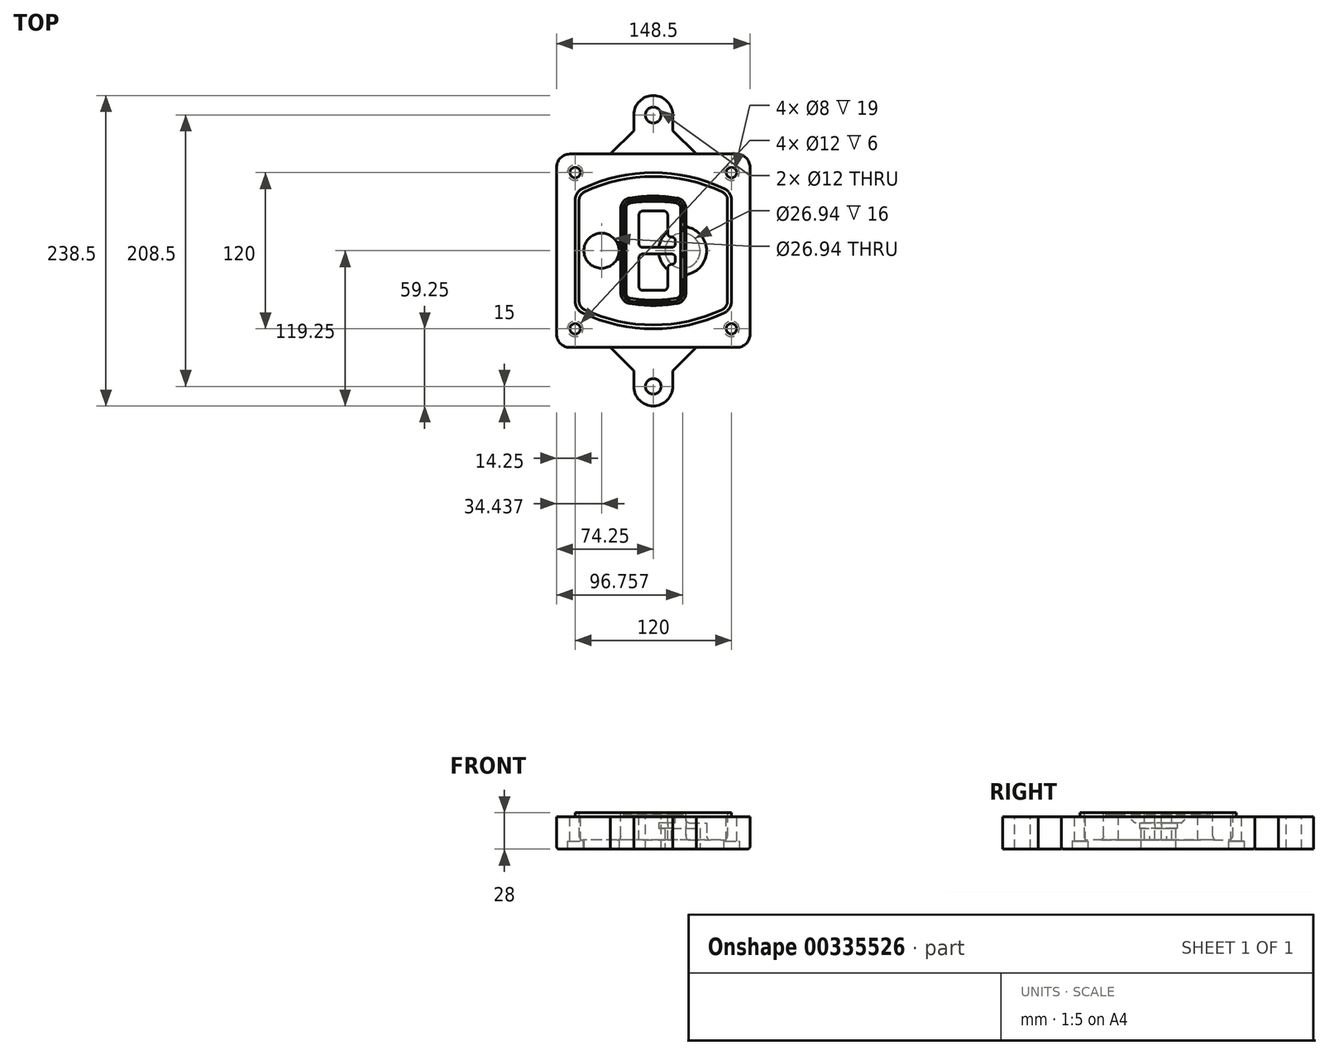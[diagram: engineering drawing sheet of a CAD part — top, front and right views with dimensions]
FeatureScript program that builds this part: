
annotation { "Feature Type Name" : "Feature", "Feature Type Description" : "" }
export const myFeature = defineFeature(function(context is Context, id is Id, definition is map)
    precondition{}
    {
        {
            var Q0;
            Q0=qCreatedBy(makeId("Top.planeOp"),FACE);
            var sketch = newSketch(context, id + "F0", { "sketchPlane" : qUnion([Q0])});
            skPoint(sketch, "E0.rect.middle", {"position": v(0, 0) * mm});
            skLineSegment(sketch, "E1.bottom", {"start": v(-64.25, -74.25) * mm, "end": v(64.25, -74.25) * mm});
            skLineSegment(sketch, "E1.top", {"start": v(-64.25, 74.25) * mm, "end": v(64.25, 74.25) * mm});
            skLineSegment(sketch, "E1.left", {"start": v(-74.25, -64.25) * mm, "end": v(-74.25, 64.25) * mm});
            skLineSegment(sketch, "E1.right", {"start": v(74.25, -64.25) * mm, "end": v(74.25, 64.25) * mm});
            skLineSegment(sketch, "E2", {"start": v(-74.25, 74.25) * mm, "end": v(74.25, -74.25) * mm, "construction": true});
            skLineSegment(sketch, "E3", {"start": v(74.25, 74.25) * mm, "end": v(-74.25, -74.25) * mm, "construction": true});
            skCircle(sketch, "E4", {"center": v(-60, 60) * mm, "radius": 4 * mm});
            skCircle(sketch, "E5", {"center": v(60, 60) * mm, "radius": 4 * mm});
            skCircle(sketch, "E6", {"center": v(60, -60) * mm, "radius": 4 * mm});
            skCircle(sketch, "E7", {"center": v(-60, -60) * mm, "radius": 4 * mm});
            skLineSegment(sketch, "E8", {"start": v(-60, 60) * mm, "end": v(60, 60) * mm, "construction": true});
            skLineSegment(sketch, "E9", {"start": v(60, 60) * mm, "end": v(60, -60) * mm, "construction": true});
            skLineSegment(sketch, "E10", {"start": v(60, -60) * mm, "end": v(-60, -60) * mm, "construction": true});
            skLineSegment(sketch, "E11", {"start": v(-60, -60) * mm, "end": v(-60, 60) * mm, "construction": true});
            skLineSegment(sketch, "E12", {"start": v(-60, 38.83) * mm, "end": v(-60, -38.83) * mm});
            skLineSegment(sketch, "E13", {"start": v(60, 38.83) * mm, "end": v(60, -38.83) * mm});
            skArc(sketch, "E14", {"start": v(54.26, 47.88) * mm, "mid": v(0, 60) * mm, "end": v(-54.26, 47.88) * mm});
            skArc(sketch, "E15", {"start": v(-54.26, -47.88) * mm, "mid": v(0, -60) * mm, "end": v(54.26, -47.88) * mm});
            skLineSegment(sketch, "E16", {"start": v(-60, 0) * mm, "end": v(60, 0) * mm, "construction": true});
            skPoint(sketch, "E17.visualSharp", {"position": v(-60, -45) * mm});
            skArc(sketch, "E17.filletArc", {"start": v(-60, -38.83) * mm, "mid": v(-58.44, -44.2) * mm, "end": v(-54.26, -47.88) * mm});
            skPoint(sketch, "E18.visualSharp", {"position": v(-60, 45) * mm});
            skArc(sketch, "E18.filletArc", {"start": v(-54.26, 47.88) * mm, "mid": v(-58.44, 44.2) * mm, "end": v(-60, 38.83) * mm});
            skPoint(sketch, "E19.visualSharp", {"position": v(60, 45) * mm});
            skArc(sketch, "E19.filletArc", {"start": v(60, 38.83) * mm, "mid": v(58.44, 44.2) * mm, "end": v(54.26, 47.88) * mm});
            skPoint(sketch, "E20.visualSharp", {"position": v(60, -45) * mm});
            skArc(sketch, "E20.filletArc", {"start": v(54.26, -47.88) * mm, "mid": v(58.44, -44.2) * mm, "end": v(60, -38.83) * mm});
            skPoint(sketch, "E21.visualSharp", {"position": v(-74.25, 74.25) * mm});
            skArc(sketch, "E21.filletArc", {"start": v(-64.25, 74.25) * mm, "mid": v(-71.32, 71.32) * mm, "end": v(-74.25, 64.25) * mm});
            skPoint(sketch, "E22.visualSharp", {"position": v(74.25, 74.25) * mm});
            skArc(sketch, "E22.filletArc", {"start": v(74.25, 64.25) * mm, "mid": v(71.32, 71.32) * mm, "end": v(64.25, 74.25) * mm});
            skPoint(sketch, "E23.visualSharp", {"position": v(74.25, -74.25) * mm});
            skArc(sketch, "E23.filletArc", {"start": v(64.25, -74.25) * mm, "mid": v(71.32, -71.32) * mm, "end": v(74.25, -64.25) * mm});
            skPoint(sketch, "E24.visualSharp", {"position": v(-74.25, -74.25) * mm});
            skArc(sketch, "E24.filletArc", {"start": v(-74.25, -64.25) * mm, "mid": v(-71.32, -71.32) * mm, "end": v(-64.25, -74.25) * mm});
            skArc(sketch, "E25.0", {"start": v(57, 38.83) * mm, "mid": v(55.9, 42.58) * mm, "end": v(52.98, 45.17) * mm});
            skLineSegment(sketch, "E25.1", {"start": v(57, 38.83) * mm, "end": v(57, -38.83) * mm});
            skArc(sketch, "E25.2", {"start": v(52.98, -45.17) * mm, "mid": v(55.9, -42.58) * mm, "end": v(57, -38.83) * mm});
            skArc(sketch, "E25.3", {"start": v(-52.98, -45.17) * mm, "mid": v(0, -57) * mm, "end": v(52.98, -45.17) * mm});
            skArc(sketch, "E25.4", {"start": v(-57, -38.83) * mm, "mid": v(-55.9, -42.58) * mm, "end": v(-52.98, -45.17) * mm});
            skArc(sketch, "E25.5", {"start": v(52.98, 45.17) * mm, "mid": v(0, 57) * mm, "end": v(-52.98, 45.17) * mm});
            skLineSegment(sketch, "E25.6", {"start": v(-57, 38.83) * mm, "end": v(-57, -38.83) * mm});
            skArc(sketch, "E25.7", {"start": v(-52.98, 45.17) * mm, "mid": v(-55.9, 42.58) * mm, "end": v(-57, 38.83) * mm});
            skArc(sketch, "E26.0", {"start": v(-55.96, 51.5) * mm, "mid": v(-61.82, 46.33) * mm, "end": v(-64, 38.83) * mm});
            skArc(sketch, "E26.1", {"start": v(55.96, 51.5) * mm, "mid": v(0, 64) * mm, "end": v(-55.96, 51.5) * mm});
            skArc(sketch, "E26.2", {"start": v(64, 38.83) * mm, "mid": v(61.82, 46.33) * mm, "end": v(55.96, 51.5) * mm});
            skLineSegment(sketch, "E26.3", {"start": v(64, 38.83) * mm, "end": v(64, -38.83) * mm});
            skArc(sketch, "E26.4", {"start": v(55.96, -51.5) * mm, "mid": v(61.82, -46.33) * mm, "end": v(64, -38.83) * mm});
            skLineSegment(sketch, "E26.5", {"start": v(-64, 38.83) * mm, "end": v(-64, -38.83) * mm});
            skArc(sketch, "E26.6", {"start": v(-55.96, -51.5) * mm, "mid": v(0, -64) * mm, "end": v(55.96, -51.5) * mm});
            skArc(sketch, "E26.7", {"start": v(-64, -38.83) * mm, "mid": v(-61.82, -46.33) * mm, "end": v(-55.96, -51.5) * mm});
            skSolve(sketch);
        }
        {
            var Q0;
            Q0=makeQuery(id+"F0.imprint","IMPRINT",FACE,{"disambiguationData":[TD([[makeQuery(id+"F0.imprint","IMPRINT",EDGE,{"derivedFrom":sQuery(id+"F0.wireOp",EDGE,"E1.bottom")}),1.0]])]});
            var Q1;
            Q1=makeQuery(id+"F0.imprint","IMPRINT",FACE,{"disambiguationData":[TD([[makeQuery(id+"F0.imprint","IMPRINT",EDGE,{"derivedFrom":sQuery(id+"F0.wireOp",EDGE,"E12")}),1.0]])]});
            var Q2;
            Q2=makeQuery(id+"F0.imprint","IMPRINT",FACE,{"disambiguationData":[TD([[makeQuery(id+"F0.imprint","IMPRINT",EDGE,{"derivedFrom":sQuery(id+"F0.wireOp",EDGE,"E25.0")}),1.0]])]});
            var Q3;
            Q3=makeQuery(id+"F0.imprint","IMPRINT",FACE,{"disambiguationData":[TD([[makeQuery(id+"F0.imprint","IMPRINT",EDGE,{"derivedFrom":sQuery(id+"F0.wireOp",EDGE,"E12")}),-1.0]])]});
            extrude(context, id + "F1", {"entities" : qUnion([Q0, Q1, Q2, Q3]), "oppositeDirection" : true, "depth" : 25 * mm});
        }
        {
            var Q0;
            Q0=makeQuery(id+"F0.imprint","IMPRINT",FACE,{"disambiguationData":[TD([[makeQuery(id+"F0.imprint","IMPRINT",EDGE,{"derivedFrom":sQuery(id+"F0.wireOp",EDGE,"E12")}),1.0]])]});
            extrude(context, id + "F2", {"entities" : qUnion([Q0]), "operationType" : NewBodyOperationType.ADD, "depth" : 3 * mm});
        }
        {
            var Q0;
            Q0=makeQuery(id+"F0.imprint","IMPRINT",FACE,{"disambiguationData":[TD([[makeQuery(id+"F0.imprint","IMPRINT",EDGE,{"derivedFrom":sQuery(id+"F0.wireOp",EDGE,"E25.0")}),1.0]])]});
            extrude(context, id + "F3", {"entities" : qUnion([Q0]), "operationType" : NewBodyOperationType.REMOVE, "oppositeDirection" : true, "depth" : 18 * mm});
        }
        {
            var Q0;
            Q0=makeQuery(id+"F2.opExtrude","CAP_FACE",FACE,{"disambiguationData":[OSD([sQuery(id+"F0.wireOp",EDGE,"E12"),sQuery(id+"F0.wireOp",EDGE,"E13"),sQuery(id+"F0.wireOp",EDGE,"E14"),sQuery(id+"F0.wireOp",EDGE,"E15"),sQuery(id+"F0.wireOp",EDGE,"E17.filletArc"),sQuery(id+"F0.wireOp",EDGE,"E18.filletArc"),sQuery(id+"F0.wireOp",EDGE,"E19.filletArc"),sQuery(id+"F0.wireOp",EDGE,"E20.filletArc"),sQuery(id+"F0.wireOp",EDGE,"E25.0"),sQuery(id+"F0.wireOp",EDGE,"E25.1"),sQuery(id+"F0.wireOp",EDGE,"E25.2"),sQuery(id+"F0.wireOp",EDGE,"E25.3"),sQuery(id+"F0.wireOp",EDGE,"E25.4"),sQuery(id+"F0.wireOp",EDGE,"E25.5"),sQuery(id+"F0.wireOp",EDGE,"E25.6"),sQuery(id+"F0.wireOp",EDGE,"E25.7")])],"isStart":false});
            var sketch = newSketch(context, id + "F4", { "sketchPlane" : qUnion([Q0])});
            skArc(sketch, "E27.0", {"start": v(-18.34, -40.45) * mm, "mid": v(0, -42) * mm, "end": v(18.34, -40.45) * mm});
            skArc(sketch, "E28.0", {"start": v(18.34, 40.45) * mm, "mid": v(0, 42) * mm, "end": v(-18.34, 40.45) * mm});
            skLineSegment(sketch, "E29", {"start": v(-25, 32.57) * mm, "end": v(-25, -32.57) * mm});
            skLineSegment(sketch, "E30", {"start": v(25, 32.57) * mm, "end": v(25, -32.57) * mm});
            skLineSegment(sketch, "E31", {"start": v(-25, 39.1) * mm, "end": v(25, 39.1) * mm, "construction": true});
            skLineSegment(sketch, "E32", {"start": v(-25, -39.1) * mm, "end": v(25, -39.1) * mm, "construction": true});
            skPoint(sketch, "E33.visualSharp", {"position": v(-25, 39.1) * mm});
            skArc(sketch, "E33.filletArc", {"start": v(-18.34, 40.45) * mm, "mid": v(-23.11, 37.73) * mm, "end": v(-25, 32.57) * mm});
            skPoint(sketch, "E34.visualSharp", {"position": v(25, 39.1) * mm});
            skArc(sketch, "E34.filletArc", {"start": v(25, 32.57) * mm, "mid": v(23.11, 37.73) * mm, "end": v(18.34, 40.45) * mm});
            skPoint(sketch, "E35.visualSharp", {"position": v(25, -39.1) * mm});
            skArc(sketch, "E35.filletArc", {"start": v(18.34, -40.45) * mm, "mid": v(23.11, -37.73) * mm, "end": v(25, -32.57) * mm});
            skPoint(sketch, "E36.visualSharp", {"position": v(-25, -39.1) * mm});
            skArc(sketch, "E36.filletArc", {"start": v(-25, -32.57) * mm, "mid": v(-23.11, -37.73) * mm, "end": v(-18.34, -40.45) * mm});
            skArc(sketch, "E37.0", {"start": v(52.98, 45.17) * mm, "mid": v(0, 57) * mm, "end": v(-52.98, 45.17) * mm});
            skArc(sketch, "E37.1", {"start": v(-52.98, 45.17) * mm, "mid": v(-55.9, 42.58) * mm, "end": v(-57, 38.83) * mm});
            skLineSegment(sketch, "E37.2", {"start": v(-57, 38.83) * mm, "end": v(-57, -38.83) * mm});
            skArc(sketch, "E37.3", {"start": v(-57, -38.83) * mm, "mid": v(-55.9, -42.58) * mm, "end": v(-52.98, -45.17) * mm});
            skArc(sketch, "E37.4", {"start": v(-52.98, -45.17) * mm, "mid": v(0, -57) * mm, "end": v(52.98, -45.17) * mm});
            skArc(sketch, "E37.5", {"start": v(52.98, -45.17) * mm, "mid": v(55.9, -42.58) * mm, "end": v(57, -38.83) * mm});
            skLineSegment(sketch, "E37.6", {"start": v(57, 38.83) * mm, "end": v(57, -38.83) * mm});
            skArc(sketch, "E37.7", {"start": v(57, 38.83) * mm, "mid": v(55.9, 42.58) * mm, "end": v(52.98, 45.17) * mm});
            skLineSegment(sketch, "E38.0", {"start": v(23, 32.57) * mm, "end": v(23, -32.57) * mm});
            skArc(sketch, "E38.1", {"start": v(18, -38.48) * mm, "mid": v(21.58, -36.44) * mm, "end": v(23, -32.57) * mm});
            skArc(sketch, "E38.2", {"start": v(-18, -38.48) * mm, "mid": v(0, -40) * mm, "end": v(18, -38.48) * mm});
            skArc(sketch, "E38.3", {"start": v(-23, -32.57) * mm, "mid": v(-21.58, -36.44) * mm, "end": v(-18, -38.48) * mm});
            skLineSegment(sketch, "E38.4", {"start": v(-23, 32.57) * mm, "end": v(-23, -32.57) * mm});
            skArc(sketch, "E38.5", {"start": v(23, 32.57) * mm, "mid": v(21.58, 36.44) * mm, "end": v(18, 38.48) * mm});
            skArc(sketch, "E38.6", {"start": v(-18, 38.48) * mm, "mid": v(-21.58, 36.44) * mm, "end": v(-23, 32.57) * mm});
            skArc(sketch, "E38.7", {"start": v(18, 38.48) * mm, "mid": v(0, 40) * mm, "end": v(-18, 38.48) * mm});
            skArc(sketch, "E39.0", {"start": v(21, 32.57) * mm, "mid": v(20.06, 35.15) * mm, "end": v(17.67, 36.5) * mm});
            skLineSegment(sketch, "E39.1", {"start": v(21, 32.57) * mm, "end": v(21, -32.57) * mm});
            skArc(sketch, "E39.2", {"start": v(17.67, -36.5) * mm, "mid": v(20.06, -35.15) * mm, "end": v(21, -32.57) * mm});
            skArc(sketch, "E39.3", {"start": v(-17.67, -36.5) * mm, "mid": v(0, -38) * mm, "end": v(17.67, -36.5) * mm});
            skArc(sketch, "E39.4", {"start": v(-21, -32.57) * mm, "mid": v(-20.06, -35.15) * mm, "end": v(-17.67, -36.5) * mm});
            skArc(sketch, "E39.5", {"start": v(17.67, 36.5) * mm, "mid": v(0, 38) * mm, "end": v(-17.67, 36.5) * mm});
            skLineSegment(sketch, "E39.6", {"start": v(-21, 32.57) * mm, "end": v(-21, -32.57) * mm});
            skArc(sketch, "E39.7", {"start": v(-17.67, 36.5) * mm, "mid": v(-20.06, 35.15) * mm, "end": v(-21, 32.57) * mm});
            skLineSegment(sketch, "E40", {"start": v(-25, 0) * mm, "end": v(25, 0) * mm, "construction": true});
            skLineSegment(sketch, "E41", {"start": v(-11, 5.5) * mm, "end": v(-11, 27.5) * mm});
            skLineSegment(sketch, "E42", {"start": v(-8, 30.5) * mm, "end": v(8, 30.5) * mm});
            skLineSegment(sketch, "E43", {"start": v(11, 27.5) * mm, "end": v(11, 13.5) * mm});
            skLineSegment(sketch, "E44", {"start": v(14, 10.5) * mm, "end": v(14, 10.5) * mm});
            skLineSegment(sketch, "E45", {"start": v(17, 7.5) * mm, "end": v(17, 5.5) * mm});
            skLineSegment(sketch, "E46", {"start": v(14, 2.5) * mm, "end": v(-8, 2.5) * mm});
            skPoint(sketch, "E47.visualSharp", {"position": v(-11, 30.5) * mm});
            skArc(sketch, "E47.filletArc", {"start": v(-8, 30.5) * mm, "mid": v(-10.12, 29.62) * mm, "end": v(-11, 27.5) * mm});
            skPoint(sketch, "E48.visualSharp", {"position": v(11, 30.5) * mm});
            skArc(sketch, "E48.filletArc", {"start": v(11, 27.5) * mm, "mid": v(10.12, 29.62) * mm, "end": v(8, 30.5) * mm});
            skPoint(sketch, "E49.visualSharp", {"position": v(11, 10.5) * mm});
            skArc(sketch, "E49.filletArc", {"start": v(11, 13.5) * mm, "mid": v(11.88, 11.38) * mm, "end": v(14, 10.5) * mm});
            skPoint(sketch, "E50.visualSharp", {"position": v(17, 10.5) * mm});
            skArc(sketch, "E50.filletArc", {"start": v(17, 7.5) * mm, "mid": v(16.12, 9.62) * mm, "end": v(14, 10.5) * mm});
            skPoint(sketch, "E51.visualSharp", {"position": v(17, 2.5) * mm});
            skArc(sketch, "E51.filletArc", {"start": v(14, 2.5) * mm, "mid": v(16.12, 3.38) * mm, "end": v(17, 5.5) * mm});
            skPoint(sketch, "E52.visualSharp", {"position": v(-11, 2.5) * mm});
            skArc(sketch, "E52.filletArc", {"start": v(-11, 5.5) * mm, "mid": v(-10.12, 3.38) * mm, "end": v(-8, 2.5) * mm});
            skLineSegment(sketch, "E53.0.MirrorCS", {"start": v(14, -2.5) * mm, "end": v(-8, -2.5) * mm});
            skArc(sketch, "E54.0.MirrorCS", {"start": v(-11, -5.5) * mm, "mid": v(-10.12, -3.38) * mm, "end": v(-8, -2.5) * mm});
            skLineSegment(sketch, "E55.0.MirrorCS", {"start": v(-11, -5.5) * mm, "end": v(-11, -27.5) * mm});
            skArc(sketch, "E56.0.MirrorCS", {"start": v(-8, -30.5) * mm, "mid": v(-10.12, -29.62) * mm, "end": v(-11, -27.5) * mm});
            skLineSegment(sketch, "E57.0.MirrorCS", {"start": v(-8, -30.5) * mm, "end": v(8, -30.5) * mm});
            skArc(sketch, "E58.0.MirrorCS", {"start": v(11, -27.5) * mm, "mid": v(10.12, -29.62) * mm, "end": v(8, -30.5) * mm});
            skLineSegment(sketch, "E59.0.MirrorCS", {"start": v(11, -27.5) * mm, "end": v(11, -13.5) * mm});
            skArc(sketch, "E60.0.MirrorCS", {"start": v(11, -13.5) * mm, "mid": v(11.88, -11.38) * mm, "end": v(14, -10.5) * mm});
            skArc(sketch, "E61.0.MirrorCS", {"start": v(17, -7.5) * mm, "mid": v(16.12, -9.62) * mm, "end": v(14, -10.5) * mm});
            skLineSegment(sketch, "E62.0.MirrorCS", {"start": v(17, -7.5) * mm, "end": v(17, -5.5) * mm});
            skArc(sketch, "E63.0.MirrorCS", {"start": v(14, -2.5) * mm, "mid": v(16.12, -3.38) * mm, "end": v(17, -5.5) * mm});
            skSolve(sketch);
        }
        {
            var Q0;
            Q0=makeQuery(id+"F4.imprint","IMPRINT",FACE,{"disambiguationData":[TD([[makeQuery(id+"F4.imprint","IMPRINT",EDGE,{"derivedFrom":sQuery(id+"F4.wireOp",EDGE,"E27.0")}),1.0]])]});
            var Q1;
            Q1=makeQuery(id+"F4.imprint","IMPRINT",FACE,{"disambiguationData":[TD([[makeQuery(id+"F4.imprint","IMPRINT",EDGE,{"derivedFrom":sQuery(id+"F4.wireOp",EDGE,"E38.0")}),-1.0]])]});
            var Q2;
            Q2=makeQuery(id+"F4.imprint","IMPRINT",FACE,{"disambiguationData":[TD([[makeQuery(id+"F4.imprint","IMPRINT",EDGE,{"derivedFrom":sQuery(id+"F4.wireOp",EDGE,"E39.0")}),1.0]])]});
            extrude(context, id + "F5", {"entities" : qUnion([Q0, Q1, Q2]), "operationType" : NewBodyOperationType.ADD, "endBound" : BoundingType.UP_TO_NEXT, "oppositeDirection" : true, "depth" : 25 * mm});
        }
        {
            var Q0;
            Q0=makeQuery(id+"F4.imprint","IMPRINT",FACE,{"disambiguationData":[TD([[makeQuery(id+"F4.imprint","IMPRINT",EDGE,{"derivedFrom":sQuery(id+"F4.wireOp",EDGE,"E38.0")}),-1.0]])]});
            extrude(context, id + "F6", {"entities" : qUnion([Q0]), "operationType" : NewBodyOperationType.REMOVE, "oppositeDirection" : true, "depth" : 2 * mm});
        }
        {
            var Q0;
            Q0=makeQuery(id+"F1.opExtrude","CAP_FACE",FACE,{"disambiguationData":[OSD([sQuery(id+"F0.wireOp",EDGE,"E1.bottom"),sQuery(id+"F0.wireOp",EDGE,"E1.top"),sQuery(id+"F0.wireOp",EDGE,"E1.left"),sQuery(id+"F0.wireOp",EDGE,"E1.right"),sQuery(id+"F0.wireOp",EDGE,"E4"),sQuery(id+"F0.wireOp",EDGE,"E5"),sQuery(id+"F0.wireOp",EDGE,"E6"),sQuery(id+"F0.wireOp",EDGE,"E7"),sQuery(id+"F0.wireOp",EDGE,"E21.filletArc"),sQuery(id+"F0.wireOp",EDGE,"E22.filletArc"),sQuery(id+"F0.wireOp",EDGE,"E23.filletArc"),sQuery(id+"F0.wireOp",EDGE,"E24.filletArc")])],"isStart":false});
            var sketch = newSketch(context, id + "F7", { "sketchPlane" : qUnion([Q0])});
            skCircle(sketch, "E64", {"center": v(22.5, 0) * mm, "radius": 13.47 * mm});
            skCircle(sketch, "E65", {"center": v(-39.81, 0) * mm, "radius": 13.47 * mm});
            skLineSegment(sketch, "E66", {"start": v(74.25, 0) * mm, "end": v(-74.25, 0) * mm});
            skCircle(sketch, "E67", {"center": v(22.5, 0) * mm, "radius": 18.47 * mm});
            skCircle(sketch, "E68", {"center": v(60, -60) * mm, "radius": 6 * mm});
            skCircle(sketch, "E69", {"center": v(-60, -60) * mm, "radius": 6 * mm});
            skCircle(sketch, "E70", {"center": v(-60, 60) * mm, "radius": 6 * mm});
            skCircle(sketch, "E71", {"center": v(60, 60) * mm, "radius": 6 * mm});
            skSolve(sketch);
        }
        {
            var Q0;
            {var subQ1=sQuery(id+"F7.wireOp",EDGE,"E66");var subQ4=sQuery(id+"F7.wireOp",EDGE,"E64");var subQ6=makeQuery(id+"F7.imprint","INTERSECT",VERTEX,{"disambiguationData":[OD(0.0)],"derivedFrom":[subQ4,subQ1]});Q0=makeQuery(id+"F7.imprint","IMPRINT",FACE,{"disambiguationData":[TD([[makeQuery(id+"F7.imprint","IMPRINT",EDGE,{"disambiguationData":[TD([[subQ6,-1.0]])],"derivedFrom":subQ4}),-1.0]])]});}
            var Q1;
            {var subQ0=sQuery(id+"F7.wireOp",EDGE,"E66");var subQ1=sQuery(id+"F7.wireOp",EDGE,"E64");var subQ3=makeQuery(id+"F7.imprint","INTERSECT",VERTEX,{"disambiguationData":[OD(0.0)],"derivedFrom":[subQ1,subQ0]});Q1=makeQuery(id+"F7.imprint","IMPRINT",FACE,{"disambiguationData":[TD([[makeQuery(id+"F7.imprint","IMPRINT",EDGE,{"disambiguationData":[TD([[subQ3,-1.0]])],"derivedFrom":subQ1}),1.0]])]});}
            var Q2;
            {var subQ0=sQuery(id+"F7.wireOp",EDGE,"E66");var subQ1=sQuery(id+"F7.wireOp",EDGE,"E64");var subQ3=makeQuery(id+"F7.imprint","INTERSECT",VERTEX,{"disambiguationData":[OD(0.0)],"derivedFrom":[subQ1,subQ0]});Q2=makeQuery(id+"F7.imprint","IMPRINT",FACE,{"disambiguationData":[TD([[makeQuery(id+"F7.imprint","IMPRINT",EDGE,{"disambiguationData":[TD([[subQ3,1.0]])],"derivedFrom":subQ1}),1.0]])]});}
            var Q3;
            {var subQ1=sQuery(id+"F7.wireOp",EDGE,"E66");var subQ4=sQuery(id+"F7.wireOp",EDGE,"E64");var subQ6=makeQuery(id+"F7.imprint","INTERSECT",VERTEX,{"disambiguationData":[OD(0.0)],"derivedFrom":[subQ4,subQ1]});Q3=makeQuery(id+"F7.imprint","IMPRINT",FACE,{"disambiguationData":[TD([[makeQuery(id+"F7.imprint","IMPRINT",EDGE,{"disambiguationData":[TD([[subQ6,1.0]])],"derivedFrom":subQ4}),-1.0]])]});}
            extrude(context, id + "F8", {"entities" : qUnion([Q0, Q1, Q2, Q3]), "operationType" : NewBodyOperationType.ADD, "oppositeDirection" : true, "depth" : 20 * mm});
        }
        {
            var Q0;
            {var subQ0=sQuery(id+"F7.wireOp",EDGE,"E66");var subQ1=sQuery(id+"F7.wireOp",EDGE,"E64");var subQ3=makeQuery(id+"F7.imprint","INTERSECT",VERTEX,{"disambiguationData":[OD(0.0)],"derivedFrom":[subQ1,subQ0]});Q0=makeQuery(id+"F7.imprint","IMPRINT",FACE,{"disambiguationData":[TD([[makeQuery(id+"F7.imprint","IMPRINT",EDGE,{"disambiguationData":[TD([[subQ3,-1.0]])],"derivedFrom":subQ1}),1.0]])]});}
            var Q1;
            {var subQ0=sQuery(id+"F7.wireOp",EDGE,"E66");var subQ1=sQuery(id+"F7.wireOp",EDGE,"E64");var subQ3=makeQuery(id+"F7.imprint","INTERSECT",VERTEX,{"disambiguationData":[OD(0.0)],"derivedFrom":[subQ1,subQ0]});Q1=makeQuery(id+"F7.imprint","IMPRINT",FACE,{"disambiguationData":[TD([[makeQuery(id+"F7.imprint","IMPRINT",EDGE,{"disambiguationData":[TD([[subQ3,1.0]])],"derivedFrom":subQ1}),1.0]])]});}
            extrude(context, id + "F9", {"entities" : qUnion([Q0, Q1]), "operationType" : NewBodyOperationType.REMOVE, "oppositeDirection" : true, "depth" : 16 * mm});
        }
        {
            var Q0;
            {var subQ0=sQuery(id+"F7.wireOp",EDGE,"E66");var subQ1=sQuery(id+"F7.wireOp",EDGE,"E65");var subQ3=makeQuery(id+"F7.imprint","INTERSECT",VERTEX,{"disambiguationData":[OD(0.0)],"derivedFrom":[subQ1,subQ0]});Q0=makeQuery(id+"F7.imprint","IMPRINT",FACE,{"disambiguationData":[TD([[makeQuery(id+"F7.imprint","IMPRINT",EDGE,{"disambiguationData":[TD([[subQ3,-1.0]])],"derivedFrom":subQ1}),1.0]])]});}
            var Q1;
            {var subQ0=sQuery(id+"F7.wireOp",EDGE,"E66");var subQ1=sQuery(id+"F7.wireOp",EDGE,"E65");var subQ3=makeQuery(id+"F7.imprint","INTERSECT",VERTEX,{"disambiguationData":[OD(0.0)],"derivedFrom":[subQ1,subQ0]});Q1=makeQuery(id+"F7.imprint","IMPRINT",FACE,{"disambiguationData":[TD([[makeQuery(id+"F7.imprint","IMPRINT",EDGE,{"disambiguationData":[TD([[subQ3,1.0]])],"derivedFrom":subQ1}),1.0]])]});}
            extrude(context, id + "F10", {"entities" : qUnion([Q0, Q1]), "operationType" : NewBodyOperationType.REMOVE, "oppositeDirection" : true, "depth" : 25 * mm});
        }
        {
            var Q0;
            Q0=makeQuery(id+"F7.imprint","IMPRINT",FACE,{"disambiguationData":[TD([[makeQuery(id+"F7.imprint","IMPRINT",EDGE,{"derivedFrom":sQuery(id+"F7.wireOp",EDGE,"E68")}),1.0]])]});
            var Q1;
            Q1=makeQuery(id+"F7.imprint","IMPRINT",FACE,{"disambiguationData":[TD([[makeQuery(id+"F7.imprint","IMPRINT",EDGE,{"derivedFrom":makeQuery(id+"F1.opExtrude","CAP_EDGE",EDGE,{"disambiguationData":[OSD([sQuery(id+"F0.wireOp",EDGE,"E5")])],"isStart":false})}),-1.0]])]});
            var Q2;
            Q2=makeQuery(id+"F7.imprint","IMPRINT",FACE,{"disambiguationData":[TD([[makeQuery(id+"F7.imprint","IMPRINT",EDGE,{"derivedFrom":sQuery(id+"F7.wireOp",EDGE,"E69")}),1.0]])]});
            var Q3;
            Q3=makeQuery(id+"F7.imprint","IMPRINT",FACE,{"disambiguationData":[TD([[makeQuery(id+"F7.imprint","IMPRINT",EDGE,{"derivedFrom":makeQuery(id+"F1.opExtrude","CAP_EDGE",EDGE,{"disambiguationData":[OSD([sQuery(id+"F0.wireOp",EDGE,"E4")])],"isStart":false})}),-1.0]])]});
            var Q4;
            Q4=makeQuery(id+"F7.imprint","IMPRINT",FACE,{"disambiguationData":[TD([[makeQuery(id+"F7.imprint","IMPRINT",EDGE,{"derivedFrom":sQuery(id+"F7.wireOp",EDGE,"E70")}),1.0]])]});
            var Q5;
            Q5=makeQuery(id+"F7.imprint","IMPRINT",FACE,{"disambiguationData":[TD([[makeQuery(id+"F7.imprint","IMPRINT",EDGE,{"derivedFrom":makeQuery(id+"F1.opExtrude","CAP_EDGE",EDGE,{"disambiguationData":[OSD([sQuery(id+"F0.wireOp",EDGE,"E7")])],"isStart":false})}),-1.0]])]});
            var Q6;
            Q6=makeQuery(id+"F7.imprint","IMPRINT",FACE,{"disambiguationData":[TD([[makeQuery(id+"F7.imprint","IMPRINT",EDGE,{"derivedFrom":sQuery(id+"F7.wireOp",EDGE,"E71")}),1.0]])]});
            var Q7;
            Q7=makeQuery(id+"F7.imprint","IMPRINT",FACE,{"disambiguationData":[TD([[makeQuery(id+"F7.imprint","IMPRINT",EDGE,{"derivedFrom":makeQuery(id+"F1.opExtrude","CAP_EDGE",EDGE,{"disambiguationData":[OSD([sQuery(id+"F0.wireOp",EDGE,"E6")])],"isStart":false})}),-1.0]])]});
            extrude(context, id + "F11", {"entities" : qUnion([Q0, Q1, Q2, Q3, Q4, Q5, Q6, Q7]), "operationType" : NewBodyOperationType.REMOVE, "oppositeDirection" : true, "depth" : 6 * mm});
        }
        {
            var Q0;
            Q0=makeQuery(id+"F9.boolean.opBoolean","COPY",FACE,{"derivedFrom":makeQuery(id+"F9.opExtrude","CAP_FACE",FACE,{"disambiguationData":[OSD([sQuery(id+"F7.wireOp",EDGE,"E64")])],"isStart":false})});
            var sketch = newSketch(context, id + "F12", { "sketchPlane" : qUnion([Q0])});
            skArc(sketch, "E72.0", {"start": v(11, 14.45) * mm, "mid": v(6.45, 9.13) * mm, "end": v(4.2, 2.5) * mm});
            skArc(sketch, "E72.1", {"start": v(4.2, -2.5) * mm, "mid": v(6.45, -9.13) * mm, "end": v(11, -14.45) * mm});
            skLineSegment(sketch, "E73", {"start": v(4.2, -2.5) * mm, "end": v(14, -2.5) * mm});
            skLineSegment(sketch, "E74.0", {"start": v(14, 2.5) * mm, "end": v(4.2, 2.5) * mm});
            skArc(sketch, "E74.1", {"start": v(14, 2.5) * mm, "mid": v(16.12, 3.38) * mm, "end": v(17, 5.5) * mm});
            skLineSegment(sketch, "E74.2", {"start": v(17, 7.5) * mm, "end": v(17, 5.5) * mm});
            skArc(sketch, "E74.3", {"start": v(17, 7.5) * mm, "mid": v(16.12, 9.62) * mm, "end": v(14, 10.5) * mm});
            skArc(sketch, "E74.4", {"start": v(11, 13.5) * mm, "mid": v(11.88, 11.38) * mm, "end": v(14, 10.5) * mm});
            skLineSegment(sketch, "E74.5", {"start": v(11, 14.45) * mm, "end": v(11, 13.5) * mm});
            skLineSegment(sketch, "E74.7", {"start": v(14, -2.5) * mm, "end": v(4.2, -2.5) * mm});
            skArc(sketch, "E74.8", {"start": v(14, -2.5) * mm, "mid": v(16.12, -3.38) * mm, "end": v(17, -5.5) * mm});
            skLineSegment(sketch, "E74.9", {"start": v(17, -7.5) * mm, "end": v(17, -5.5) * mm});
            skArc(sketch, "E74.10", {"start": v(17, -7.5) * mm, "mid": v(16.12, -9.62) * mm, "end": v(14, -10.5) * mm});
            skArc(sketch, "E74.11", {"start": v(11, -13.5) * mm, "mid": v(11.88, -11.38) * mm, "end": v(14, -10.5) * mm});
            skLineSegment(sketch, "E74.12", {"start": v(11, -14.45) * mm, "end": v(11, -13.5) * mm});
            skPoint(sketch, "E75.orphan", {"position": v(11, -27.5) * mm});
            skPoint(sketch, "E76.orphan", {"position": v(-8, -2.5) * mm});
            skPoint(sketch, "E77.orphan", {"position": v(-8, 2.5) * mm});
            skPoint(sketch, "E78.orphan", {"position": v(11, 27.5) * mm});
            skSolve(sketch);
        }
        {
            var Q0;
            {var subQ7=sQuery(id+"F12.wireOp",EDGE,"E72.0");var subQ14=sQuery(id+"F12.wireOp",EDGE,"E72.1");var subQ16=sQuery(id+"F12.wireOp",EDGE,"E74.1");var subQ18=sQuery(id+"F12.wireOp",EDGE,"E74.8");Q0=qUnion([makeQuery(id+"F12.imprint","IMPRINT",FACE,{"disambiguationData":[TD([[makeQuery(id+"F12.imprint","IMPRINT",EDGE,{"derivedFrom":subQ7}),1.0]])]}),makeQuery(id+"F12.imprint","IMPRINT",FACE,{"disambiguationData":[TD([[makeQuery(id+"F12.imprint","IMPRINT",EDGE,{"derivedFrom":subQ14}),1.0]])]}),makeQuery(id+"F12.imprint","IMPRINT",FACE,{"disambiguationData":[TD([[makeQuery(id+"F12.imprint","IMPRINT",EDGE,{"derivedFrom":subQ16}),1.0]])]}),makeQuery(id+"F12.imprint","IMPRINT",FACE,{"disambiguationData":[TD([[makeQuery(id+"F12.imprint","IMPRINT",EDGE,{"derivedFrom":subQ18}),-1.0]])]})]);}
            var Q1;
            Q1=makeQuery(id+"F5.boolean.opBoolean","SPLIT",FACE,{"disambiguationData":[TD([makeQuery(id+"F5.opExtrude","SWEPT_FACE",FACE,{"disambiguationData":[OSD([sQuery(id+"F4.wireOp",EDGE,"E41")])]})])],"derivedFrom":makeQuery(id+"F3.boolean.opBoolean","COPY",FACE,{"derivedFrom":makeQuery(id+"F3.opExtrude","CAP_FACE",FACE,{"disambiguationData":[OSD([sQuery(id+"F0.wireOp",EDGE,"E25.0"),sQuery(id+"F0.wireOp",EDGE,"E25.1"),sQuery(id+"F0.wireOp",EDGE,"E25.2"),sQuery(id+"F0.wireOp",EDGE,"E25.3"),sQuery(id+"F0.wireOp",EDGE,"E25.4"),sQuery(id+"F0.wireOp",EDGE,"E25.5"),sQuery(id+"F0.wireOp",EDGE,"E25.6"),sQuery(id+"F0.wireOp",EDGE,"E25.7")])],"isStart":false})})});
            extrude(context, id + "F13", {"entities" : qUnion([Q0]), "operationType" : NewBodyOperationType.REMOVE, "endBound" : BoundingType.UP_TO_SURFACE, "endBoundEntityFace" : qUnion([Q1]), "depth" : 25 * mm});
        }
        {
            var Q0;
            Q0=makeQuery(id+"F3.boolean.opBoolean","COPY",EDGE,{"derivedFrom":makeQuery(id+"F3.opExtrude","CAP_EDGE",EDGE,{"disambiguationData":[OSD([sQuery(id+"F0.wireOp",EDGE,"E25.6")])],"isStart":false})});
            var Q1;
            Q1=makeQuery(id+"F8.boolean.opBoolean","INTERSECT",EDGE,{"derivedFrom":[makeQuery(id+"F5.opExtrude","SWEPT_FACE",FACE,{"disambiguationData":[OSD([sQuery(id+"F4.wireOp",EDGE,"E30")])]}),makeQuery(id+"F8.opExtrude","CAP_FACE",FACE,{"disambiguationData":[OSD([sQuery(id+"F7.wireOp",EDGE,"E67")])],"isStart":false})]});
            var Q2;
            Q2=makeQuery(id+"F8.boolean.opBoolean","INTERSECT",EDGE,{"disambiguationData":[OD(1.0)],"derivedFrom":[makeQuery(id+"F5.opExtrude","SWEPT_FACE",FACE,{"disambiguationData":[OSD([sQuery(id+"F4.wireOp",EDGE,"E30")])]}),makeQuery(id+"F8.opExtrude","SWEPT_FACE",FACE,{"disambiguationData":[OSD([sQuery(id+"F7.wireOp",EDGE,"E67")])]})]});
            var Q3;
            {var subQ0=sQuery(id+"F4.wireOp",EDGE,"E30");Q3=makeQuery(id+"F8.boolean.opBoolean","SPLIT",EDGE,{"disambiguationData":[TD([makeQuery(id+"F5.opExtrude","SWEPT_FACE",FACE,{"disambiguationData":[OSD([sQuery(id+"F4.wireOp",EDGE,"E35.filletArc")])]})])],"derivedFrom":makeQuery(id+"F5.opExtrude","CAP_EDGE",EDGE,{"disambiguationData":[OSD([subQ0])],"isStart":false})});}
            var Q4;
            {var subQ0=sQuery(id+"F0.wireOp",EDGE,"E25.7");var subQ1=sQuery(id+"F0.wireOp",EDGE,"E25.1");var subQ2=sQuery(id+"F0.wireOp",EDGE,"E25.6");var subQ3=sQuery(id+"F0.wireOp",EDGE,"E25.5");var subQ4=sQuery(id+"F0.wireOp",EDGE,"E25.4");var subQ5=sQuery(id+"F0.wireOp",EDGE,"E25.0");var subQ6=sQuery(id+"F0.wireOp",EDGE,"E25.2");var subQ7=sQuery(id+"F0.wireOp",EDGE,"E25.3");Q4=makeQuery(id+"F8.boolean.opBoolean","INTERSECT",EDGE,{"derivedFrom":[makeQuery(id+"F5.boolean.opBoolean","SPLIT",FACE,{"disambiguationData":[TD([makeQuery(id+"F2.opExtrude","SWEPT_FACE",FACE,{"disambiguationData":[OSD([subQ5])]})])],"derivedFrom":makeQuery(id+"F3.boolean.opBoolean","COPY",FACE,{"derivedFrom":makeQuery(id+"F3.opExtrude","CAP_FACE",FACE,{"disambiguationData":[OSD([subQ5,subQ1,subQ6,subQ7,subQ4,subQ3,subQ2,subQ0])],"isStart":false})})}),makeQuery(id+"F8.opExtrude","SWEPT_FACE",FACE,{"disambiguationData":[OSD([sQuery(id+"F7.wireOp",EDGE,"E67")])]})]});}
            var Q5;
            Q5=makeQuery(id+"F8.boolean.opBoolean","INTERSECT",EDGE,{"disambiguationData":[OD(0.0)],"derivedFrom":[makeQuery(id+"F5.opExtrude","SWEPT_FACE",FACE,{"disambiguationData":[OSD([sQuery(id+"F4.wireOp",EDGE,"E30")])]}),makeQuery(id+"F8.opExtrude","SWEPT_FACE",FACE,{"disambiguationData":[OSD([sQuery(id+"F7.wireOp",EDGE,"E67")])]})]});
            fillet(context, id + "F14", {"entities" : qUnion([Q0, Q1, Q2, Q3, Q4, Q5]), "radius" : 3 * mm, "tangentPropagation" : true, "allowEdgeOverflow" : false});
        }
        {
            var Q0;
            Q0=makeQuery(id+"F1.opExtrude","CAP_EDGE",EDGE,{"disambiguationData":[OSD([sQuery(id+"F0.wireOp",EDGE,"E1.bottom")])],"isStart":false});
            fillet(context, id + "F15", {"entities" : qUnion([Q0]), "radius" : 2 * mm, "tangentPropagation" : true, "allowEdgeOverflow" : false});
        }
        {
            var Q0;
            {var subQ0=sQuery(id+"F0.wireOp",EDGE,"E21.filletArc");var subQ1=sQuery(id+"F0.wireOp",EDGE,"E7");var subQ2=sQuery(id+"F0.wireOp",EDGE,"E6");var subQ3=sQuery(id+"F0.wireOp",EDGE,"E5");var subQ4=sQuery(id+"F0.wireOp",EDGE,"E4");var subQ5=sQuery(id+"F0.wireOp",EDGE,"E22.filletArc");var subQ6=sQuery(id+"F0.wireOp",EDGE,"E1.bottom");var subQ7=sQuery(id+"F0.wireOp",EDGE,"E1.right");var subQ8=sQuery(id+"F0.wireOp",EDGE,"E1.top");var subQ9=sQuery(id+"F0.wireOp",EDGE,"E1.left");var subQ10=sQuery(id+"F0.wireOp",EDGE,"E23.filletArc");var subQ11=sQuery(id+"F0.wireOp",EDGE,"E24.filletArc");Q0=makeQuery(id+"F2.boolean.opBoolean","SPLIT",FACE,{"disambiguationData":[TD([makeQuery(id+"F1.opExtrude","SWEPT_FACE",FACE,{"disambiguationData":[OSD([subQ6])]})])],"derivedFrom":makeQuery(id+"F1.opExtrude","CAP_FACE",FACE,{"disambiguationData":[OSD([subQ6,subQ8,subQ9,subQ7,subQ4,subQ3,subQ2,subQ1,subQ0,subQ5,subQ10,subQ11])],"isStart":true})});}
            var sketch = newSketch(context, id + "F16", { "sketchPlane" : qUnion([Q0])});
            skLineSegment(sketch, "E79", {"start": v(-33, 74.25) * mm, "end": v(-15, 92.25) * mm});
            skLineSegment(sketch, "E80", {"start": v(-15, 92.25) * mm, "end": v(-15, 104.25) * mm});
            skLineSegment(sketch, "E81", {"start": v(33, 74.25) * mm, "end": v(15, 92.25) * mm});
            skLineSegment(sketch, "E82", {"start": v(15, 92.25) * mm, "end": v(15, 104.25) * mm});
            skArc(sketch, "E83", {"start": v(15, 104.25) * mm, "mid": v(0, 119.25) * mm, "end": v(-15, 104.25) * mm});
            skLineSegment(sketch, "E84", {"start": v(0, 104.25) * mm, "end": v(0, 74.25) * mm, "construction": true});
            skCircle(sketch, "E85", {"center": v(0, 104.25) * mm, "radius": 6 * mm});
            skLineSegment(sketch, "E86", {"start": v(-74.25, 0) * mm, "end": v(74.25, 0) * mm, "construction": true});
            skLineSegment(sketch, "E87.MirrorCS", {"start": v(15, -92.25) * mm, "end": v(15, -104.25) * mm});
            skCircle(sketch, "E88.MirrorC", {"center": v(0, -104.25) * mm, "radius": 6 * mm});
            skLineSegment(sketch, "E89.MirrorCS", {"start": v(33, -74.25) * mm, "end": v(15, -92.25) * mm});
            skLineSegment(sketch, "E90.MirrorCS", {"start": v(-33, -74.25) * mm, "end": v(-15, -92.25) * mm});
            skLineSegment(sketch, "E91.MirrorCS", {"start": v(-15, -92.25) * mm, "end": v(-15, -104.25) * mm});
            skArc(sketch, "E92.MirrorCS", {"start": v(15, -104.25) * mm, "mid": v(0, -119.25) * mm, "end": v(-15, -104.25) * mm});
            skLineSegment(sketch, "E93.MirrorCS", {"start": v(0, -104.25) * mm, "end": v(0, -74.25) * mm, "construction": true});
            skSolve(sketch);
        }
        {
            var Q0;
            {var subQ1=sQuery(id+"F16.wireOp",EDGE,"E79");Q0=makeQuery(id+"F16.imprint","IMPRINT",FACE,{"disambiguationData":[TD([[makeQuery(id+"F16.imprint","IMPRINT",EDGE,{"derivedFrom":subQ1}),-1.0]])]});}
            var Q1;
            Q1=makeQuery(id+"F16.imprint","IMPRINT",FACE,{"disambiguationData":[TD([[makeQuery(id+"F16.imprint","IMPRINT",EDGE,{"derivedFrom":sQuery(id+"F16.wireOp",EDGE,"E87.MirrorCS")}),-1.0]])]});
            extrude(context, id + "F17", {"entities" : qUnion([Q0, Q1]), "oppositeDirection" : true, "depth" : 25 * mm});
        }
    });
